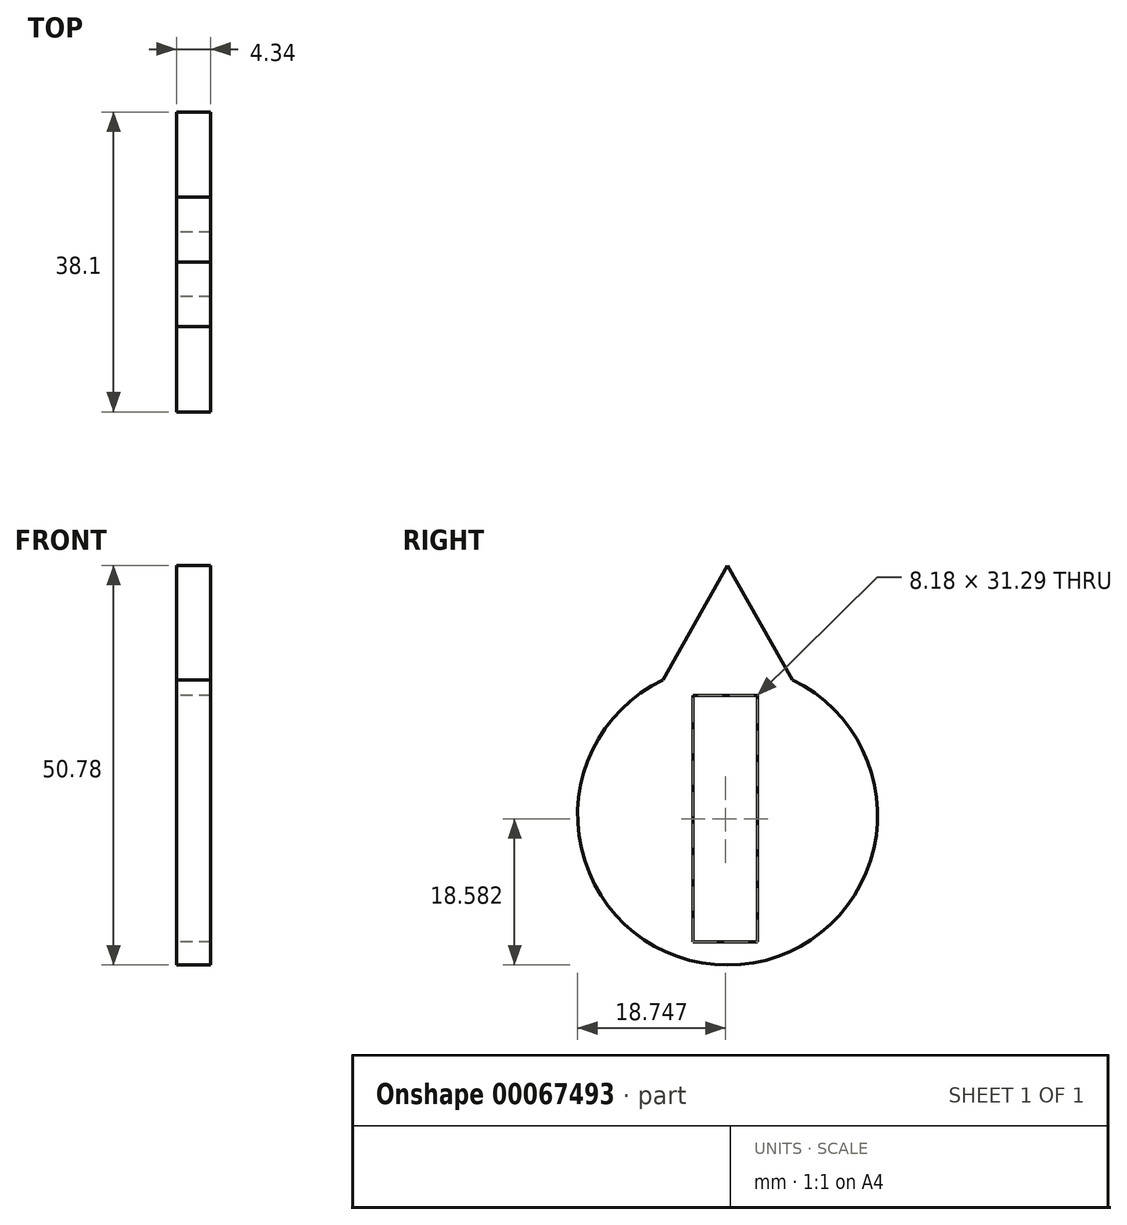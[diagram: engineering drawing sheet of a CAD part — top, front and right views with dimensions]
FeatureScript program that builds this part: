
annotation { "Feature Type Name" : "Feature", "Feature Type Description" : "" }
export const myFeature = defineFeature(function(context is Context, id is Id, definition is map)
    precondition{}
    {
        {
            var Q0;
            Q0=qCreatedBy(makeId("Right.planeOp"),FACE);
            var sketch = newSketch(context, id + "F0", { "sketchPlane" : qUnion([Q0])});
            skLineSegment(sketch, "E0", {"start": v(-39.27, 14.9) * mm, "end": v(-31.1, 14.9) * mm});
            skLineSegment(sketch, "E1", {"start": v(-39.27, 14.9) * mm, "end": v(-39.27, -16.38) * mm});
            skLineSegment(sketch, "E2", {"start": v(-31.1, 14.9) * mm, "end": v(-31.1, -16.38) * mm});
            skLineSegment(sketch, "E3", {"start": v(-31.1, -16.38) * mm, "end": v(-39.27, -16.38) * mm});
            skPoint(sketch, "E4.end.orphan", {"position": v(-36.84, -10.4) * mm});
            skPoint(sketch, "E4.start.orphan", {"position": v(-35.18, 14.9) * mm});
            skArc(sketch, "E5", {"start": v(-43.12, 16.9) * mm, "mid": v(-34.88, -19.32) * mm, "end": v(-26.64, 16.9) * mm});
            skPoint(sketch, "E6.start.orphan", {"position": v(-42.1, 17.35) * mm});
            skPoint(sketch, "E7.end.orphan", {"position": v(-40.84, 18.21) * mm});
            skPoint(sketch, "E8.start.orphan", {"position": v(-31.94, -19.1) * mm});
            skPoint(sketch, "E9.orphan", {"position": v(-53.93, 0) * mm});
            skLineSegment(sketch, "E10.trimOffspring", {"start": v(-53.73, 2.44) * mm, "end": v(-53.93, 3.51) * mm, "construction": true});
            skPoint(sketch, "E11.end.orphan", {"position": v(-42.1, -16.38) * mm});
            skPoint(sketch, "E12.start.orphan", {"position": v(-38.64, -0.74) * mm});
            skLineSegment(sketch, "E13", {"start": v(-34.88, -1.36) * mm, "end": v(-34.88, 33.56) * mm});
            skPoint(sketch, "E14.start.orphan", {"position": v(-35.74, 33.56) * mm});
            skLineSegment(sketch, "E15", {"start": v(-43.12, 16.9) * mm, "end": v(-34.88, 31.46) * mm});
            skLineSegment(sketch, "E16.MirrorCS", {"start": v(-26.64, 16.9) * mm, "end": v(-34.88, 31.46) * mm});
            skPoint(sketch, "E17.orphan", {"position": v(-39.48, 18.21) * mm});
            skSolve(sketch);
        }
        {
            var Q0;
            Q0 = qSketchRegion(id + "F0", true);
            extrude(context, id + "F1", {"entities" : qUnion([Q0]), "depth" : 4.34 * mm});
        }
    });
